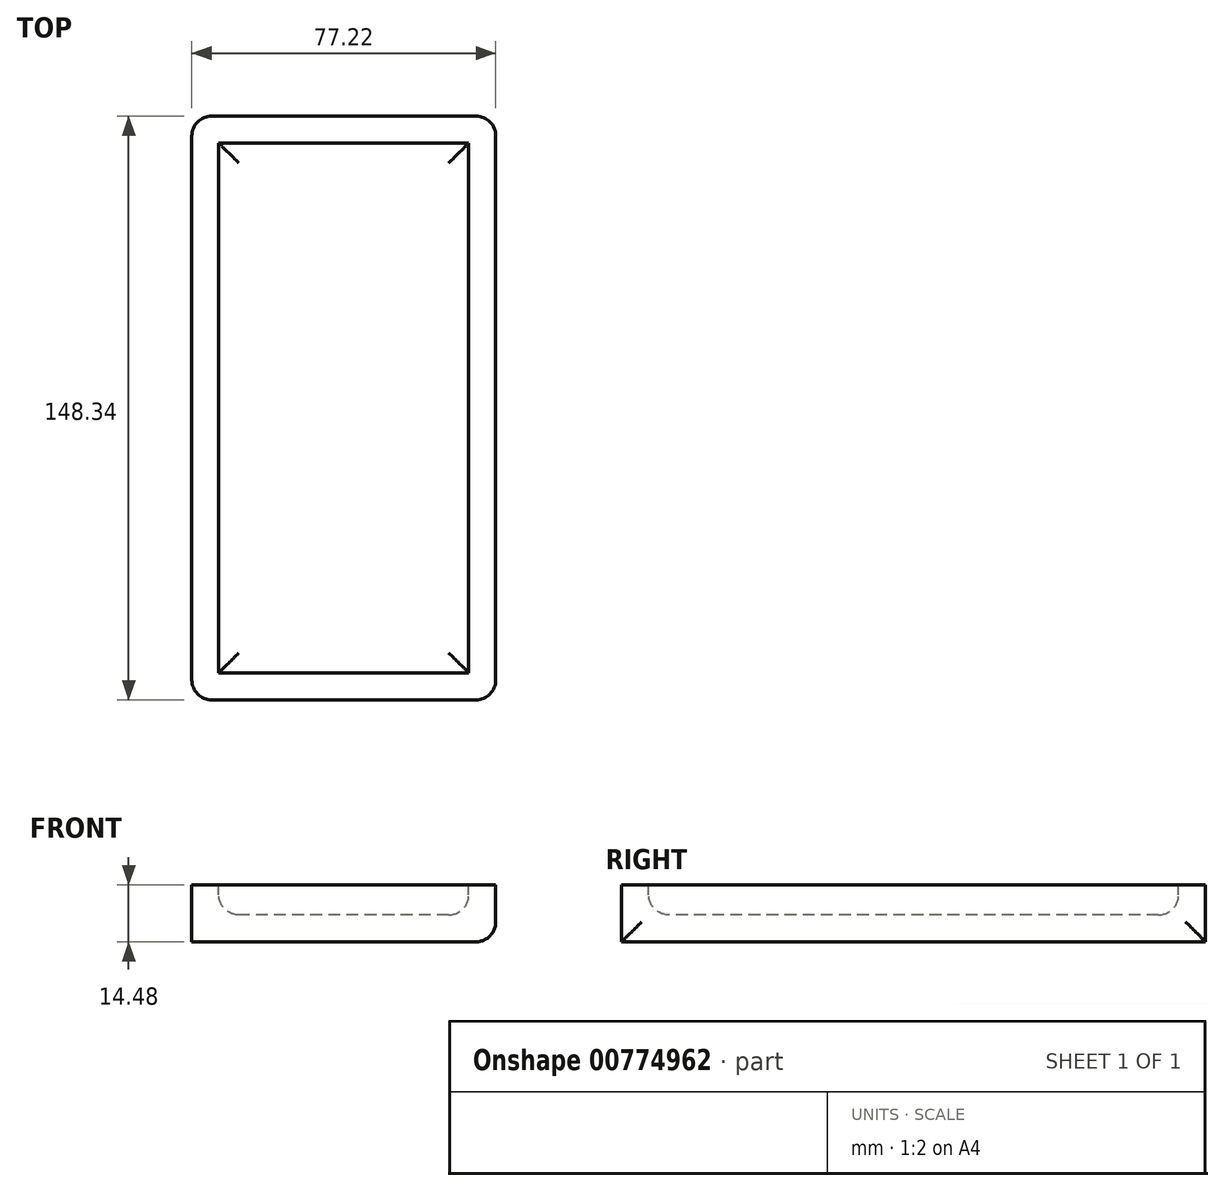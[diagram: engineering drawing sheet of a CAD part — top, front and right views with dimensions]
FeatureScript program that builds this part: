
annotation { "Feature Type Name" : "Feature", "Feature Type Description" : "" }
export const myFeature = defineFeature(function(context is Context, id is Id, definition is map)
    precondition{}
    {
        {
            var Q0;
            Q0=qCreatedBy(makeId("Top.planeOp"),FACE);
            var sketch = newSketch(context, id + "F0", { "sketchPlane" : qUnion([Q0])});
            skLineSegment(sketch, "E0.bottom", {"start": v(38.6, 74.17) * mm, "end": v(-38.6, 74.17) * mm});
            skLineSegment(sketch, "E0.top", {"start": v(38.6, -74.17) * mm, "end": v(-38.6, -74.17) * mm});
            skLineSegment(sketch, "E0.left", {"start": v(38.6, 74.17) * mm, "end": v(38.6, -74.17) * mm});
            skLineSegment(sketch, "E0.right", {"start": v(-38.6, 74.17) * mm, "end": v(-38.6, -74.17) * mm});
            skPoint(sketch, "E0.middle", {"position": v(0, 0) * mm});
            skSolve(sketch);
        }
        {
            var Q0;
            Q0=makeQuery(id+"F0.imprint","IMPRINT",FACE,{"disambiguationData":[TD([[makeQuery(id+"F0.imprint","IMPRINT",EDGE,{"derivedFrom":sQuery(id+"F0.wireOp",EDGE,"E0.bottom")}),1.0]])]});
            extrude(context, id + "F1", {"entities" : qUnion([Q0]), "depth" : 14.48 * mm, "offsetDistance" : 25.4 * mm});
        }
        {
            var Q0;
            Q0=makeQuery(id+"F1.opExtrude","SWEPT_EDGE",EDGE,{"disambiguationData":[OSD([sQuery(id+"F0.wireOp",EDGE,"E0.bottom"),sQuery(id+"F0.wireOp",EDGE,"E0.right")])]});
            var Q1;
            Q1=makeQuery(id+"F1.opExtrude","SWEPT_EDGE",EDGE,{"disambiguationData":[OSD([sQuery(id+"F0.wireOp",EDGE,"E0.bottom"),sQuery(id+"F0.wireOp",EDGE,"E0.left")])]});
            var Q2;
            Q2=makeQuery(id+"F1.opExtrude","SWEPT_EDGE",EDGE,{"disambiguationData":[OSD([sQuery(id+"F0.wireOp",EDGE,"E0.top"),sQuery(id+"F0.wireOp",EDGE,"E0.left")])]});
            var Q3;
            Q3=makeQuery(id+"F1.opExtrude","SWEPT_EDGE",EDGE,{"disambiguationData":[OSD([sQuery(id+"F0.wireOp",EDGE,"E0.top"),sQuery(id+"F0.wireOp",EDGE,"E0.right")])]});
            var Q4;
            Q4=makeQuery(id+"F1.opExtrude","CAP_EDGE",EDGE,{"disambiguationData":[OSD([sQuery(id+"F0.wireOp",EDGE,"E0.left")])],"isStart":true});
            fillet(context, id + "F2", {"entities" : qUnion([Q0, Q1, Q2, Q3, Q4]), "radius" : 5.08 * mm, "tangentPropagation" : true, "allowEdgeOverflow" : false});
        }
        {
            var Q0;
            Q0=makeQuery(id+"F1.opExtrude","CAP_FACE",FACE,{"disambiguationData":[OSD([sQuery(id+"F0.wireOp",EDGE,"E0.bottom"),sQuery(id+"F0.wireOp",EDGE,"E0.top"),sQuery(id+"F0.wireOp",EDGE,"E0.left"),sQuery(id+"F0.wireOp",EDGE,"E0.right")])],"isStart":false});
            shell(context, id + "F3", {"entities" : qUnion([Q0]), "thickness" : 6.86 * mm});
        }
        {
            var Q0;
            Q0=makeQuery(id+"F3.opShell","OFFSET_FACE",FACE,{"disambiguationData":[OSD([sQuery(id+"F0.wireOp",EDGE,"E0.bottom"),sQuery(id+"F0.wireOp",EDGE,"E0.top"),sQuery(id+"F0.wireOp",EDGE,"E0.left"),sQuery(id+"F0.wireOp",EDGE,"E0.right")])]});
            fillet(context, id + "F4", {"entities" : qUnion([Q0]), "radius" : 5.08 * mm, "tangentPropagation" : true, "allowEdgeOverflow" : false});
        }
    });
